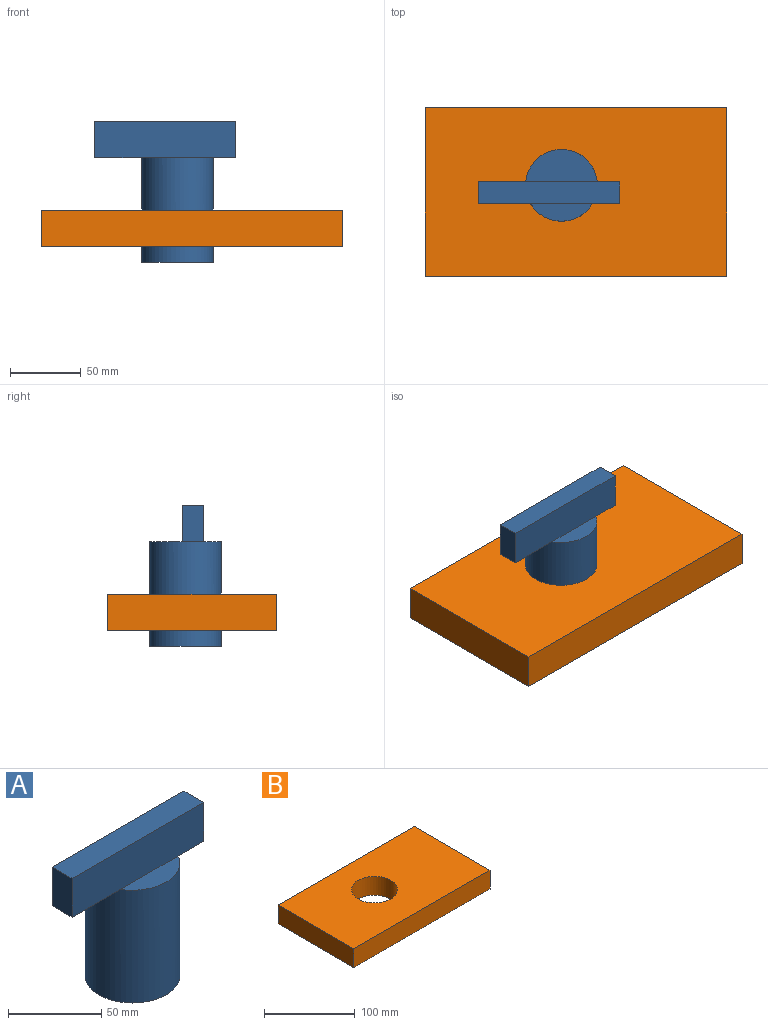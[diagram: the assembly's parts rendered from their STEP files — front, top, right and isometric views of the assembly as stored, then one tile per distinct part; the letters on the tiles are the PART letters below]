
ASSEMBLY  parts=2 mates=1
PART A: 11 faces, bbox 99.7x50.7x99.3 mm
  f0: plane 50.48x23.05mm, normal (0,0,1), area 892.9mm2, adj f1,f9
  f1: cylinder r=25.35mm len=73.91mm, axis (0,0,-1), area 11770.6mm2, adj f0,f2,f3,f4,f5
  f2: plane 43.84x12.62mm, normal (0,0,1), area 392.2mm2, adj f1,f7
  f3: plane 50.69x50.69mm, normal (0,0,-1), area 2018.1mm2, adj f1
  f4: plane 36.57x15.02mm, normal (0,0,-1), area 512mm2, adj f1,f6,f7,f9
  f5: plane 19.3x15.02mm, normal (0,0,-1), area 252.6mm2, adj f1,f7,f8,f9
  f6: plane 25.4x15.02mm, normal (-1,0,0), area 381.5mm2, adj f4,f7,f9,f10
  f7: plane 99.7x25.4mm, normal (0,-1,0), area 2532.5mm2, adj f2,f4,f5,f6,f8,f10
  f8: plane 25.4x15.02mm, normal (1,0,0), area 381.5mm2, adj f5,f7,f9,f10
  f9: plane 99.7x25.4mm, normal (0,1,0), area 2532.5mm2, adj f0,f4,f5,f6,f8,f10
  f10: plane 99.7x15.02mm, normal (0,0,1), area 1497.5mm2, adj f6,f7,f8,f9
PART B: 7 faces, bbox 212.5x118.7x25.4 mm
  f0: plane 212.47x25.4mm, normal (0,1,0), area 5396.8mm2, adj f1,f4,f5,f6
  f1: plane 118.67x25.4mm, normal (-1,0,0), area 3014.2mm2, adj f0,f2,f5,f6
  f2: plane 212.47x25.4mm, normal (0,-1,0), area 5396.8mm2, adj f1,f4,f5,f6
  f3: cylinder r=25.35mm len=50.69mm, axis (0,0,-1), area 4044.9mm2, adj f5,f6
  f4: plane 118.67x25.4mm, normal (1,0,0), area 3014.2mm2, adj f0,f2,f5,f6
  f5: plane 212.47x118.67mm, normal (0,0,1), area 23196.4mm2, adj f0,f1,f2,f3,f4
  f6: plane 212.47x118.67mm, normal (0,0,-1), area 23196.4mm2, adj f0,f1,f2,f3,f4
PLACE A t=(-39.86,20,-36.96)mm
PLACE B t=(-39.86,20,0)mm fixed
MATE cylindrical B.f3 <-> A.f1  axis (0,0,1) through (-87.15,25.12,25.4)mm
